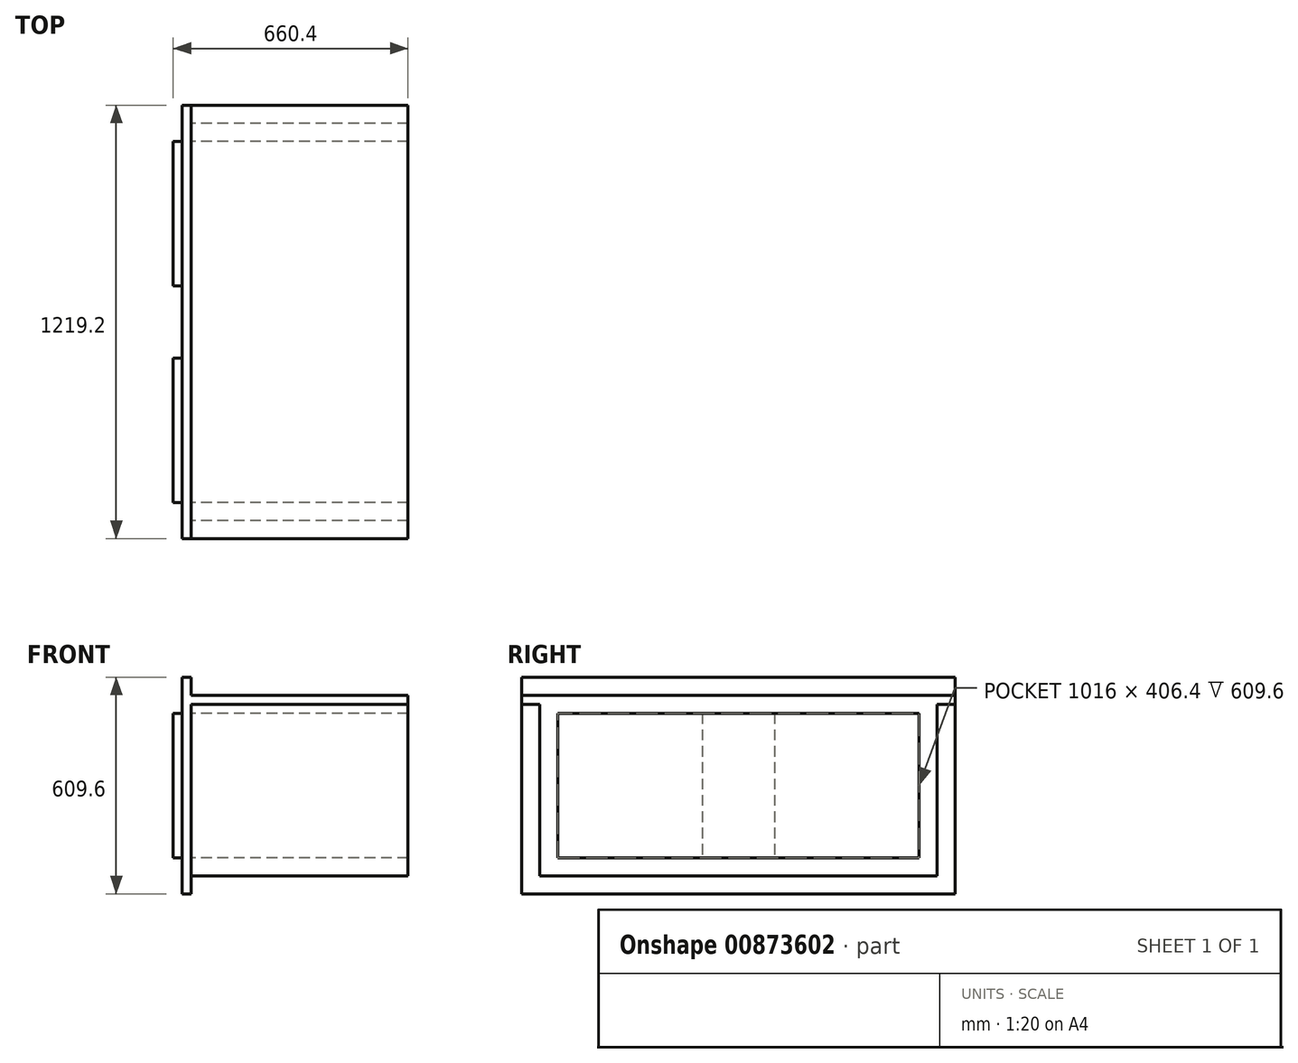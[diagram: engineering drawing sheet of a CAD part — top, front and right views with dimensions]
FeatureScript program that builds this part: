
annotation { "Feature Type Name" : "Feature", "Feature Type Description" : "" }
export const myFeature = defineFeature(function(context is Context, id is Id, definition is map)
    precondition{}
    {
        {
            var Q0;
            Q0=qCreatedBy(makeId("Top.planeOp"),FACE);
            var sketch = newSketch(context, id + "F0", { "sketchPlane" : qUnion([Q0])});
            skLineSegment(sketch, "E0.bottom", {"start": v(0, 0) * mm, "end": v(25.4, 0) * mm});
            skLineSegment(sketch, "E0.top", {"start": v(0, 1219.2) * mm, "end": v(25.4, 1219.2) * mm});
            skLineSegment(sketch, "E0.left", {"start": v(0, 0) * mm, "end": v(0, 1219.2) * mm});
            skLineSegment(sketch, "E1", {"start": v(-103.16, 609.6) * mm, "end": v(0, 609.6) * mm, "construction": true});
            skPoint(sketch, "E1.startSnap0", {"position": v(0, 609.6) * mm});
            skLineSegment(sketch, "E2.trimOffspring", {"start": v(50.8, 609.6) * mm, "end": v(198.06, 609.6) * mm, "construction": true});
            skLineSegment(sketch, "E3", {"start": v(25.4, 1219.2) * mm, "end": v(25.4, 0) * mm});
            skSolve(sketch);
        }
        {
            var Q0;
            Q0 = qSketchRegion(id + "F0", true);
            extrude(context, id + "F1", {"entities" : qUnion([Q0]), "depth" : 609.6 * mm, "offsetDistance" : 25.4 * mm});
        }
        {
            var Q0;
            Q0=makeQuery(id+"F1.opExtrude","SWEPT_FACE",FACE,{"disambiguationData":[OSD([sQuery(id+"F0.wireOp",EDGE,"E3")])]});
            var sketch = newSketch(context, id + "F2", { "sketchPlane" : qUnion([Q0])});
            skLineSegment(sketch, "E4.0", {"start": v(50.8, 558.8) * mm, "end": v(1168.4, 558.8) * mm});
            skLineSegment(sketch, "E4.1", {"start": v(50.8, 558.8) * mm, "end": v(50.8, 50.8) * mm});
            skLineSegment(sketch, "E4.2", {"start": v(50.8, 50.8) * mm, "end": v(1168.4, 50.8) * mm});
            skLineSegment(sketch, "E4.3", {"start": v(1168.4, 558.8) * mm, "end": v(1168.4, 50.8) * mm});
            skLineSegment(sketch, "E5.0", {"start": v(101.6, 508) * mm, "end": v(1117.6, 508) * mm});
            skLineSegment(sketch, "E5.1", {"start": v(101.6, 508) * mm, "end": v(101.6, 101.6) * mm});
            skLineSegment(sketch, "E5.2", {"start": v(101.6, 101.6) * mm, "end": v(1117.6, 101.6) * mm});
            skLineSegment(sketch, "E5.3", {"start": v(1117.6, 508) * mm, "end": v(1117.6, 101.6) * mm});
            skSolve(sketch);
        }
        {
            var Q0;
            Q0 = qSketchRegion(id + "F2", true);
            extrude(context, id + "F3", {"entities" : qUnion([Q0]), "operationType" : NewBodyOperationType.ADD, "depth" : 609.6 * mm, "offsetDistance" : 25.4 * mm});
        }
        {
            var Q0;
            Q0=makeQuery(id+"F1.opExtrude","SWEPT_FACE",FACE,{"disambiguationData":[OSD([sQuery(id+"F0.wireOp",EDGE,"E0.left")])]});
            var sketch = newSketch(context, id + "F4", { "sketchPlane" : qUnion([Q0])});
            skPoint(sketch, "E6.startSnap0", {"position": v(-609.6, 0) * mm});
            skPoint(sketch, "E7.middle", {"position": v(-609.6, 304.8) * mm});
            skLineSegment(sketch, "E8.0", {"start": v(-1117.6, 508) * mm, "end": v(-711.2, 508) * mm});
            skLineSegment(sketch, "E8.1", {"start": v(-1117.6, 508) * mm, "end": v(-1117.6, 101.6) * mm});
            skLineSegment(sketch, "E8.2", {"start": v(-1117.6, 101.6) * mm, "end": v(-711.2, 101.6) * mm});
            skLineSegment(sketch, "E8.3", {"start": v(-711.2, 508) * mm, "end": v(-711.2, 101.6) * mm});
            skLineSegment(sketch, "E9", {"start": v(-609.6, 0) * mm, "end": v(-609.6, 716.79) * mm, "construction": true});
            skLineSegment(sketch, "E10.MirrorCS", {"start": v(-508, 508) * mm, "end": v(-508, 101.6) * mm});
            skLineSegment(sketch, "E11.MirrorCS", {"start": v(-101.6, 508) * mm, "end": v(-101.6, 101.6) * mm});
            skLineSegment(sketch, "E12.MirrorCS", {"start": v(-101.6, 508) * mm, "end": v(-508, 508) * mm});
            skLineSegment(sketch, "E13.MirrorCS", {"start": v(-101.6, 101.6) * mm, "end": v(-508, 101.6) * mm});
            skSolve(sketch);
        }
        {
            var Q0;
            Q0 = qSketchRegion(id + "F4", true);
            extrude(context, id + "F5", {"entities" : qUnion([Q0]), "operationType" : NewBodyOperationType.ADD, "depth" : 25.4 * mm, "offsetDistance" : 25.4 * mm});
        }
        {
            var Q0;
            Q0=makeQuery(id+"F3.opExtrude","SWEPT_FACE",FACE,{"disambiguationData":[OSD([sQuery(id+"F2.wireOp",EDGE,"E4.1")])]});
            var sketch = newSketch(context, id + "F6", { "sketchPlane" : qUnion([Q0])});
            skLineSegment(sketch, "E14.bottom", {"start": v(635, 558.8) * mm, "end": v(25.4, 558.8) * mm});
            skLineSegment(sketch, "E14.top", {"start": v(635, 533.4) * mm, "end": v(25.4, 533.4) * mm});
            skLineSegment(sketch, "E14.left", {"start": v(635, 558.8) * mm, "end": v(635, 533.4) * mm});
            skLineSegment(sketch, "E14.right", {"start": v(25.4, 558.8) * mm, "end": v(25.4, 523.94) * mm});
            skSolve(sketch);
        }
        {
            var Q0;
            Q0 = qSketchRegion(id + "F6", true);
            extrude(context, id + "F7", {"entities" : qUnion([Q0]), "operationType" : NewBodyOperationType.ADD, "depth" : 50.8 * mm, "offsetDistance" : 25.4 * mm});
        }
        {
            var Q0;
            Q0=makeQuery(id+"F3.opExtrude","SWEPT_FACE",FACE,{"disambiguationData":[OSD([sQuery(id+"F2.wireOp",EDGE,"E4.3")])]});
            var sketch = newSketch(context, id + "F8", { "sketchPlane" : qUnion([Q0])});
            skLineSegment(sketch, "E15.bottom", {"start": v(-635, 558.8) * mm, "end": v(-25.4, 558.8) * mm});
            skLineSegment(sketch, "E15.top", {"start": v(-635, 533.4) * mm, "end": v(-25.4, 533.4) * mm});
            skLineSegment(sketch, "E15.left", {"start": v(-635, 558.8) * mm, "end": v(-635, 533.4) * mm});
            skLineSegment(sketch, "E15.right", {"start": v(-25.4, 558.8) * mm, "end": v(-25.4, 533.4) * mm});
            skSolve(sketch);
        }
        {
            var Q0;
            Q0 = qSketchRegion(id + "F8", true);
            extrude(context, id + "F9", {"entities" : qUnion([Q0]), "operationType" : NewBodyOperationType.ADD, "depth" : 50.8 * mm, "offsetDistance" : 25.4 * mm});
        }
    });
